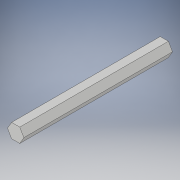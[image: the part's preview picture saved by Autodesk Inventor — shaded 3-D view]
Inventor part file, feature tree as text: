
AUTODESK INVENTOR PART (.ipt)
format: ipt  version: 2018 (Build 220112000, 112)  size: 95,232 bytes
history: native  units: in
note: dims shown in document units (in); Inventor stores cm internally (conversion verified against a paired STEP export)
features: extrude x1, sketch x1
ambient origin geometry x8: Origin, YZ Plane, XZ Plane, XY Plane, X Axis, Y Axis, Z Axis, Center Point
bodies: Solid1 (feature_tree)
feature tree (2):
  extrude  "Extrusion1"  Depth=0.5in
  sketch  "Sketch1"  dims[d1=5.25in d2=0.0in d3=0.5in]
